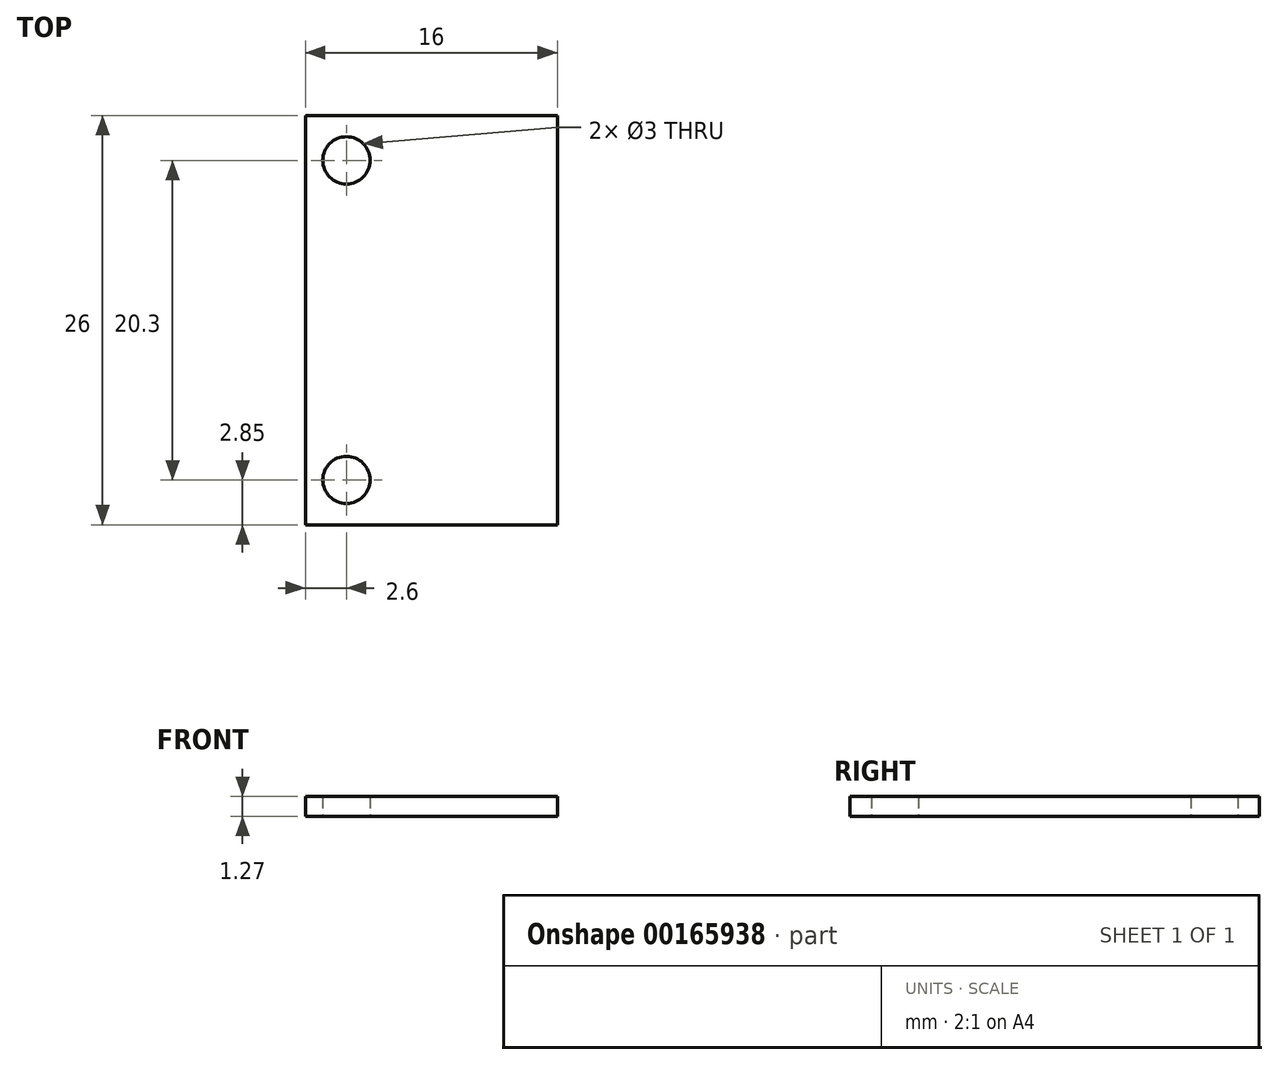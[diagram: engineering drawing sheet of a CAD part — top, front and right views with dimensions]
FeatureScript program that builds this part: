
annotation { "Feature Type Name" : "Feature", "Feature Type Description" : "" }
export const myFeature = defineFeature(function(context is Context, id is Id, definition is map)
    precondition{}
    {
        {
            var Q0;
            Q0=qCreatedBy(makeId("Top.planeOp"),FACE);
            var sketch = newSketch(context, id + "F0", { "sketchPlane" : qUnion([Q0])});
            skLineSegment(sketch, "E0.bottom", {"start": v(-8, 13) * mm, "end": v(8, 13) * mm});
            skLineSegment(sketch, "E0.top", {"start": v(-8, -13) * mm, "end": v(8, -13) * mm});
            skLineSegment(sketch, "E0.left", {"start": v(-8, 13) * mm, "end": v(-8, -13) * mm});
            skLineSegment(sketch, "E0.right", {"start": v(8, 13) * mm, "end": v(8, -13) * mm});
            skLineSegment(sketch, "E1", {"start": v(-8, 0) * mm, "end": v(8, 0) * mm, "construction": true});
            skPoint(sketch, "E2", {"position": v(0, 0) * mm});
            skCircle(sketch, "E3", {"center": v(-5.4, 10.15) * mm, "radius": 1.5 * mm});
            skCircle(sketch, "E4", {"center": v(-5.4, -10.15) * mm, "radius": 1.5 * mm});
            skLineSegment(sketch, "E5", {"start": v(-5.4, 10.15) * mm, "end": v(-5.4, -10.15) * mm, "construction": true});
            skPoint(sketch, "E6", {"position": v(-5.4, 0) * mm});
            skSolve(sketch);
        }
        {
            var Q0;
            Q0 = qSketchRegion(id + "F0", true);
            extrude(context, id + "F1", {"entities" : qUnion([Q0]), "depth" : 1.27 * mm});
        }
    });
